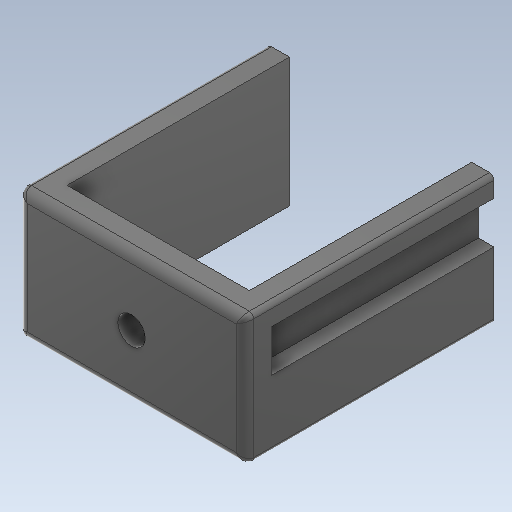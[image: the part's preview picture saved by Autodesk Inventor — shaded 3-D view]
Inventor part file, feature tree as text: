
AUTODESK INVENTOR PART (.ipt)
format: ipt  version: 2020 (Build 240168000, 168)  size: 559,616 bytes
history: native  units: mm
features: extrude x10, projected_geometry x7, sketch x5, fillet x4
ambient origin geometry x8: Origin, YZ Plane, XZ Plane, XY Plane, X Axis, Y Axis, Z Axis, Center Point
bodies: Body1 (feature_tree)
feature tree (26):
  extrude  "Выдавливание7"  Depth=4.0mm
  extrude  "Выдавливание16"  Depth=25.5mm
  sketch  "Эскиз12"
  extrude  "Выдавливание17"  Depth=3.0mm
  extrude  "Выдавливание18"  Depth=3.0mm
  extrude  "Выдавливание19"  Depth=3.0mm
  fillet  "Сопряжение1"  Radius=20.2mm
  extrude  "Выдавливание20"  Depth=14.0mm TaperAngle=0.0deg
  fillet  "Сопряжение2"  Radius=26.0mm
  extrude  "Выдавливание21"  Depth=20.5mm
  extrude  "Выдавливание22"  Depth=3.0mm
  extrude  "Выдавливание23"  Depth=1.5mm
  extrude  "Выдавливание24"  Depth=0.5mm
  fillet  "Сопряжение3"  Radius=0.5mm
  fillet  "Сопряжение4"  Radius=0.5mm
  sketch  "Эскиз1"
  sketch  "Эскиз10"
  projected_geometry  "Спроецированная петля9"
  projected_geometry  "Спроецированная петля10"
  projected_geometry  "Спроецированная петля11"
  projected_geometry  "Спроецированная петля12"
  projected_geometry  "Спроецированная петля13"
  sketch  "Эскиз14"
  projected_geometry  "Спроецированная петля15"
  sketch  "Эскиз16"
  projected_geometry  "Спроецированная петля16"
